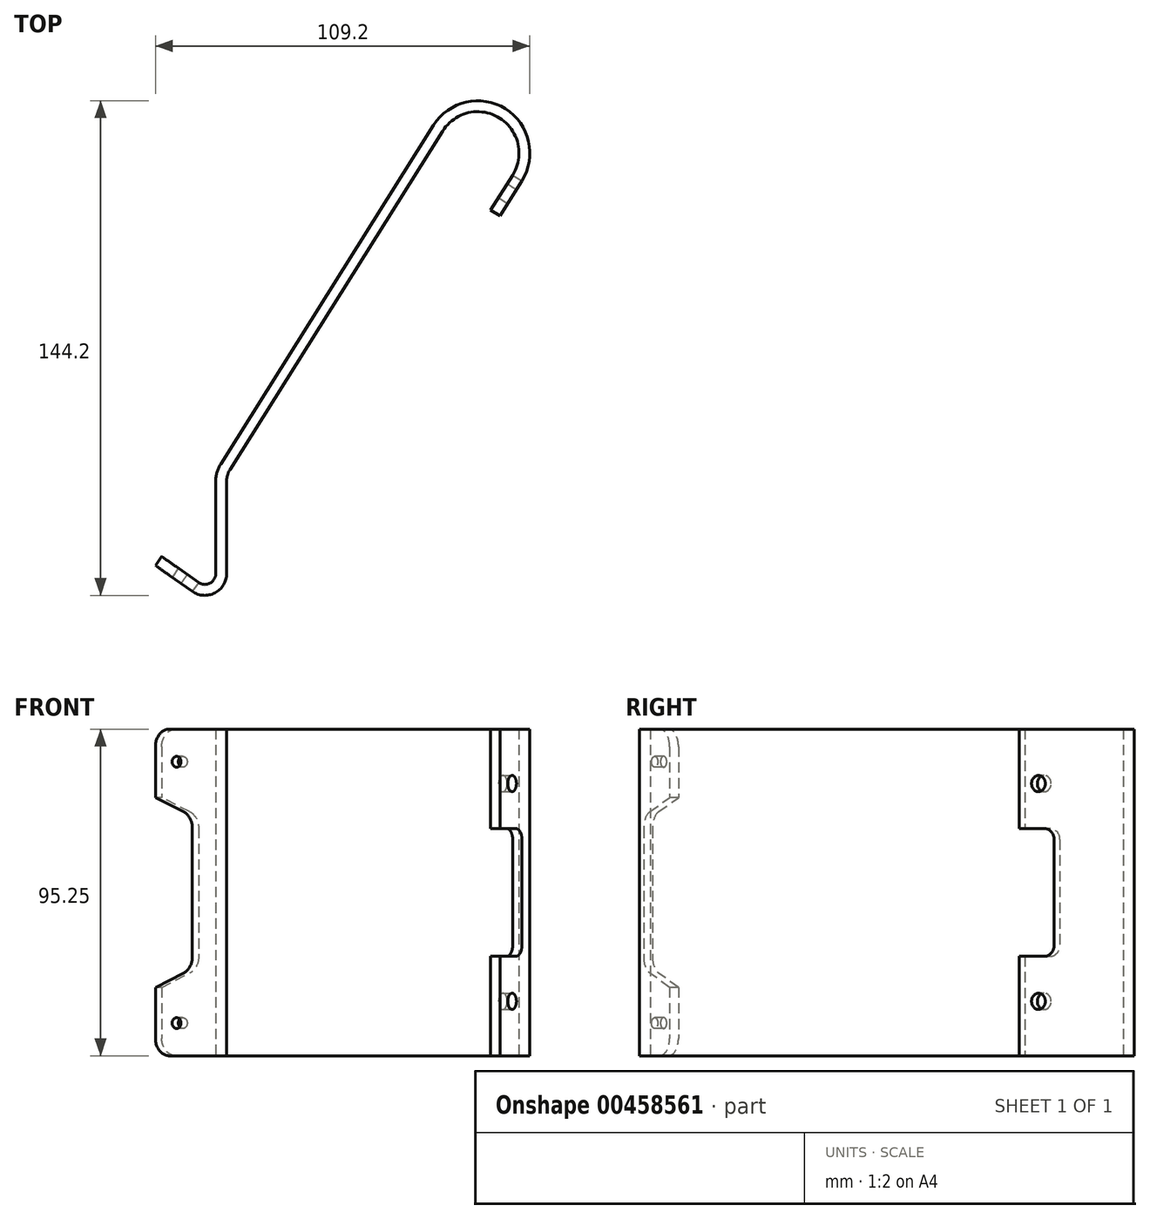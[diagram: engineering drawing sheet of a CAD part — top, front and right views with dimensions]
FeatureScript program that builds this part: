
annotation { "Feature Type Name" : "Feature", "Feature Type Description" : "" }
export const myFeature = defineFeature(function(context is Context, id is Id, definition is map)
    precondition{}
    {
        {
            var Q0;
            Q0=qCreatedBy(makeId("Top.planeOp"),FACE);
            var sketch = newSketch(context, id + "F0", { "sketchPlane" : qUnion([Q0])});
            skLineSegment(sketch, "E0", {"start": v(-93.96, -120.22) * mm, "end": v(-83.21, -127.8) * mm});
            skLineSegment(sketch, "E1", {"start": v(-73.2, -122.61) * mm, "end": v(-73.2, -95.68) * mm});
            skLineSegment(sketch, "E2", {"start": v(-72.23, -92.3) * mm, "end": v(-10.22, 6.42) * mm});
            skArc(sketch, "E3", {"start": v(10.22, -6.42) * mm, "mid": v(6.42, 10.22) * mm, "end": v(-10.22, 6.42) * mm});
            skLineSegment(sketch, "E4", {"start": v(10.22, -6.42) * mm, "end": v(3.8, -16.63) * mm});
            skPoint(sketch, "E5.visualSharp", {"position": v(-73.2, -93.85) * mm});
            skArc(sketch, "E5.filletArc", {"start": v(-72.23, -92.3) * mm, "mid": v(-72.95, -93.92) * mm, "end": v(-73.2, -95.68) * mm});
            skPoint(sketch, "E6.visualSharp", {"position": v(-73.2, -134.86) * mm});
            skArc(sketch, "E6.filletArc", {"start": v(-83.21, -127.8) * mm, "mid": v(-76.63, -128.25) * mm, "end": v(-73.2, -122.61) * mm});
            skArc(sketch, "E7.1", {"start": v(12.9, -8.1) * mm, "mid": v(8.1, 12.9) * mm, "end": v(-12.9, 8.1) * mm});
            skLineSegment(sketch, "E7.2", {"start": v(-74.92, -90.61) * mm, "end": v(-12.9, 8.1) * mm});
            skLineSegment(sketch, "E7.3", {"start": v(-92.13, -117.63) * mm, "end": v(-81.38, -125.2) * mm});
            skArc(sketch, "E7.4", {"start": v(-81.38, -125.2) * mm, "mid": v(-78.1, -125.43) * mm, "end": v(-76.38, -122.61) * mm});
            skLineSegment(sketch, "E7.5", {"start": v(-76.38, -122.61) * mm, "end": v(-76.38, -95.68) * mm});
            skArc(sketch, "E7.6", {"start": v(-74.92, -90.61) * mm, "mid": v(-76, -93.04) * mm, "end": v(-76.38, -95.68) * mm});
            skLineSegment(sketch, "E8", {"start": v(-93.96, -120.22) * mm, "end": v(-92.13, -117.63) * mm});
            skLineSegment(sketch, "E9.0", {"start": v(12.9, -8.1) * mm, "end": v(6.49, -18.32) * mm});
            skLineSegment(sketch, "E10", {"start": v(3.8, -16.63) * mm, "end": v(6.49, -18.32) * mm});
            skPoint(sketch, "E11.orphan", {"position": v(-2.62, -26.85) * mm});
            skSolve(sketch);
        }
        {
            var Q0;
            Q0 = qSketchRegion(id + "F0", true);
            extrude(context, id + "F1", {"entities" : qUnion([Q0]), "depth" : 95.25 * mm, "offsetDistance" : 25.4 * mm});
        }
        {
            var Q0;
            Q0=makeQuery(id+"F1.opExtrude","SWEPT_FACE",FACE,{"disambiguationData":[OSD([sQuery(id+"F0.wireOp",EDGE,"E0")])]});
            var sketch = newSketch(context, id + "F2", { "sketchPlane" : qUnion([Q0])});
            skCircle(sketch, "E12", {"center": v(0, 85.73) * mm, "radius": 1.59 * mm});
            skCircle(sketch, "E13", {"center": v(0, 9.53) * mm, "radius": 1.59 * mm});
            skLineSegment(sketch, "E14", {"start": v(0, 85.73) * mm, "end": v(0, 9.53) * mm, "construction": true});
            skLineSegment(sketch, "E15.0", {"start": v(-7.53, 75.3) * mm, "end": v(-7.53, 19.95) * mm});
            skLineSegment(sketch, "E16", {"start": v(-7.53, 95.25) * mm, "end": v(-7.53, 0) * mm});
            skLineSegment(sketch, "E17", {"start": v(-7.53, 47.63) * mm, "end": v(20.98, 47.63) * mm, "construction": true});
            skLineSegment(sketch, "E18", {"start": v(-7.53, 19.95) * mm, "end": v(5.62, 25.4) * mm});
            skLineSegment(sketch, "E19", {"start": v(5.62, 25.4) * mm, "end": v(5.62, 69.85) * mm});
            skLineSegment(sketch, "E20", {"start": v(5.62, 69.85) * mm, "end": v(-7.53, 75.3) * mm});
            skSolve(sketch);
        }
        {
            var Q0;
            Q0=makeQuery(id+"F2.imprint","IMPRINT",FACE,{"disambiguationData":[TD([[makeQuery(id+"F2.imprint","IMPRINT",EDGE,{"derivedFrom":sQuery(id+"F2.wireOp",EDGE,"E12")}),1.0]])]});
            var Q1;
            Q1=makeQuery(id+"F2.imprint","IMPRINT",FACE,{"disambiguationData":[TD([[makeQuery(id+"F2.imprint","IMPRINT",EDGE,{"derivedFrom":sQuery(id+"F2.wireOp",EDGE,"E13")}),1.0]])]});
            var Q2;
            Q2=makeQuery(id+"F1.opExtrude","SWEPT_FACE",FACE,{"disambiguationData":[OSD([sQuery(id+"F0.wireOp",EDGE,"E7.3")])]});
            extrude(context, id + "F3", {"entities" : qUnion([Q0, Q1]), "operationType" : NewBodyOperationType.REMOVE, "endBound" : BoundingType.UP_TO_SURFACE, "oppositeDirection" : true, "depth" : 25.4 * mm, "endBoundEntityFace" : qUnion([Q2]), "offsetDistance" : 25.4 * mm});
        }
        {
            var Q0;
            {var subQ0=sQuery(id+"F2.wireOp",EDGE,"E18");Q0=makeQuery(id+"F2.imprint","IMPRINT",FACE,{"disambiguationData":[TD([[makeQuery(id+"F2.imprint","IMPRINT",EDGE,{"derivedFrom":subQ0}),1.0]])]});}
            var Q1;
            Q1=makeQuery(id+"F1.opExtrude","SWEPT_FACE",FACE,{"disambiguationData":[OSD([sQuery(id+"F0.wireOp",EDGE,"E7.3")])]});
            extrude(context, id + "F4", {"entities" : qUnion([Q0]), "operationType" : NewBodyOperationType.REMOVE, "endBound" : BoundingType.UP_TO_SURFACE, "oppositeDirection" : true, "depth" : 25.4 * mm, "endBoundEntityFace" : qUnion([Q1]), "offsetDistance" : 25.4 * mm});
        }
        {
            var Q0;
            Q0=makeQuery(id+"F1.opExtrude","CAP_EDGE",EDGE,{"disambiguationData":[OSD([sQuery(id+"F0.wireOp",EDGE,"E8")])],"isStart":false});
            var Q1;
            Q1=makeQuery(id+"F4.boolean.opBoolean","COPY",EDGE,{"derivedFrom":makeQuery(id+"F4.opExtrude","SWEPT_EDGE",EDGE,{"disambiguationData":[OSD([sQuery(id+"F2.wireOp",EDGE,"E16"),sQuery(id+"F2.wireOp",EDGE,"E20")])]})});
            var Q2;
            Q2=makeQuery(id+"F4.boolean.opBoolean","COPY",EDGE,{"derivedFrom":makeQuery(id+"F4.opExtrude","SWEPT_EDGE",EDGE,{"disambiguationData":[OSD([sQuery(id+"F0.wireOp",EDGE,"E0"),sQuery(id+"F0.wireOp",EDGE,"E6.filletArc"),sQuery(id+"F2.wireOp",EDGE,"E19"),sQuery(id+"F2.wireOp",EDGE,"E20")])]})});
            var Q3;
            Q3=makeQuery(id+"F4.boolean.opBoolean","COPY",EDGE,{"derivedFrom":makeQuery(id+"F4.opExtrude","SWEPT_EDGE",EDGE,{"disambiguationData":[OSD([sQuery(id+"F0.wireOp",EDGE,"E0"),sQuery(id+"F0.wireOp",EDGE,"E6.filletArc"),sQuery(id+"F2.wireOp",EDGE,"E18"),sQuery(id+"F2.wireOp",EDGE,"E19")])]})});
            var Q4;
            Q4=makeQuery(id+"F4.boolean.opBoolean","COPY",EDGE,{"derivedFrom":makeQuery(id+"F4.opExtrude","SWEPT_EDGE",EDGE,{"disambiguationData":[OSD([sQuery(id+"F2.wireOp",EDGE,"E16"),sQuery(id+"F2.wireOp",EDGE,"E18")])]})});
            var Q5;
            Q5=makeQuery(id+"F1.opExtrude","CAP_EDGE",EDGE,{"disambiguationData":[OSD([sQuery(id+"F0.wireOp",EDGE,"E8")])],"isStart":true});
            fillet(context, id + "F5", {"entities" : qUnion([Q0, Q1, Q2, Q3, Q4, Q5]), "tangentPropagation" : true, "radius" : 5.08 * mm, "defaultsChanged" : false, "vertexSettings" : [], "allowEdgeOverflow" : false});
        }
        {
            var Q0;
            Q0=makeQuery(id+"F1.opExtrude","SWEPT_FACE",FACE,{"disambiguationData":[OSD([sQuery(id+"F0.wireOp",EDGE,"E9.0")])]});
            var sketch = newSketch(context, id + "F6", { "sketchPlane" : qUnion([Q0])});
            skCircle(sketch, "E21", {"center": v(-5.38, 79.38) * mm, "radius": 2.38 * mm});
            skLineSegment(sketch, "E22", {"start": v(-5.38, 79.38) * mm, "end": v(-5.38, 15.88) * mm, "construction": true});
            skCircle(sketch, "E23", {"center": v(-5.38, 15.88) * mm, "radius": 2.38 * mm});
            skLineSegment(sketch, "E24", {"start": v(-12.06, 95.25) * mm, "end": v(-12.06, 0) * mm, "construction": true});
            skLineSegment(sketch, "E25", {"start": v(-12.06, 47.63) * mm, "end": v(9.69, 47.63) * mm, "construction": true});
            skSolve(sketch);
        }
        {
            var Q0;
            Q0=makeQuery(id+"F6.imprint","IMPRINT",FACE,{"disambiguationData":[TD([[makeQuery(id+"F6.imprint","IMPRINT",EDGE,{"derivedFrom":sQuery(id+"F6.wireOp",EDGE,"E21")}),1.0]])]});
            var Q1;
            Q1=makeQuery(id+"F6.imprint","IMPRINT",FACE,{"disambiguationData":[TD([[makeQuery(id+"F6.imprint","IMPRINT",EDGE,{"derivedFrom":sQuery(id+"F6.wireOp",EDGE,"E23")}),1.0]])]});
            var Q2;
            Q2=makeQuery(id+"F1.opExtrude","SWEPT_FACE",FACE,{"disambiguationData":[OSD([sQuery(id+"F0.wireOp",EDGE,"E4")])]});
            extrude(context, id + "F7", {"entities" : qUnion([Q0, Q1]), "operationType" : NewBodyOperationType.REMOVE, "endBound" : BoundingType.UP_TO_SURFACE, "oppositeDirection" : true, "depth" : 25.4 * mm, "endBoundEntityFace" : qUnion([Q2]), "offsetDistance" : 25.4 * mm});
        }
        {
            var Q0;
            Q0=makeQuery(id+"F1.opExtrude","SWEPT_FACE",FACE,{"disambiguationData":[OSD([sQuery(id+"F0.wireOp",EDGE,"E9.0")])]});
            var sketch = newSketch(context, id + "F8", { "sketchPlane" : qUnion([Q0])});
            skLineSegment(sketch, "E26.bottom", {"start": v(-12.06, 66.23) * mm, "end": v(-3.18, 66.23) * mm});
            skLineSegment(sketch, "E26.top", {"start": v(-12.06, 29.02) * mm, "end": v(-3.17, 29.02) * mm});
            skLineSegment(sketch, "E26.left", {"start": v(-12.06, 66.23) * mm, "end": v(-12.06, 29.02) * mm});
            skLineSegment(sketch, "E26.right", {"start": v(0, 63.05) * mm, "end": v(0, 32.2) * mm});
            skLineSegment(sketch, "E27", {"start": v(-5.38, 79.38) * mm, "end": v(-5.38, 15.88) * mm, "construction": true});
            skLineSegment(sketch, "E28", {"start": v(-5.38, 47.62) * mm, "end": v(-26.5, 47.62) * mm, "construction": true});
            skPoint(sketch, "E29.visualSharp", {"position": v(0, 66.23) * mm});
            skArc(sketch, "E29.filletArc", {"start": v(0, 63.05) * mm, "mid": v(-0.93, 65.3) * mm, "end": v(-3.18, 66.23) * mm});
            skPoint(sketch, "E30.visualSharp", {"position": v(0, 29.02) * mm});
            skArc(sketch, "E30.filletArc", {"start": v(-3.17, 29.02) * mm, "mid": v(-0.93, 29.95) * mm, "end": v(0, 32.2) * mm});
            skSolve(sketch);
        }
        {
            var Q0;
            Q0=makeQuery(id+"F8.imprint","IMPRINT",FACE,{"disambiguationData":[TD([[makeQuery(id+"F8.imprint","IMPRINT",EDGE,{"derivedFrom":sQuery(id+"F8.wireOp",EDGE,"E26.bottom")}),-1.0]])]});
            extrude(context, id + "F9", {"entities" : qUnion([Q0]), "operationType" : NewBodyOperationType.REMOVE, "oppositeDirection" : true, "depth" : 12.7 * mm, "offsetDistance" : 25.4 * mm});
        }
    });
